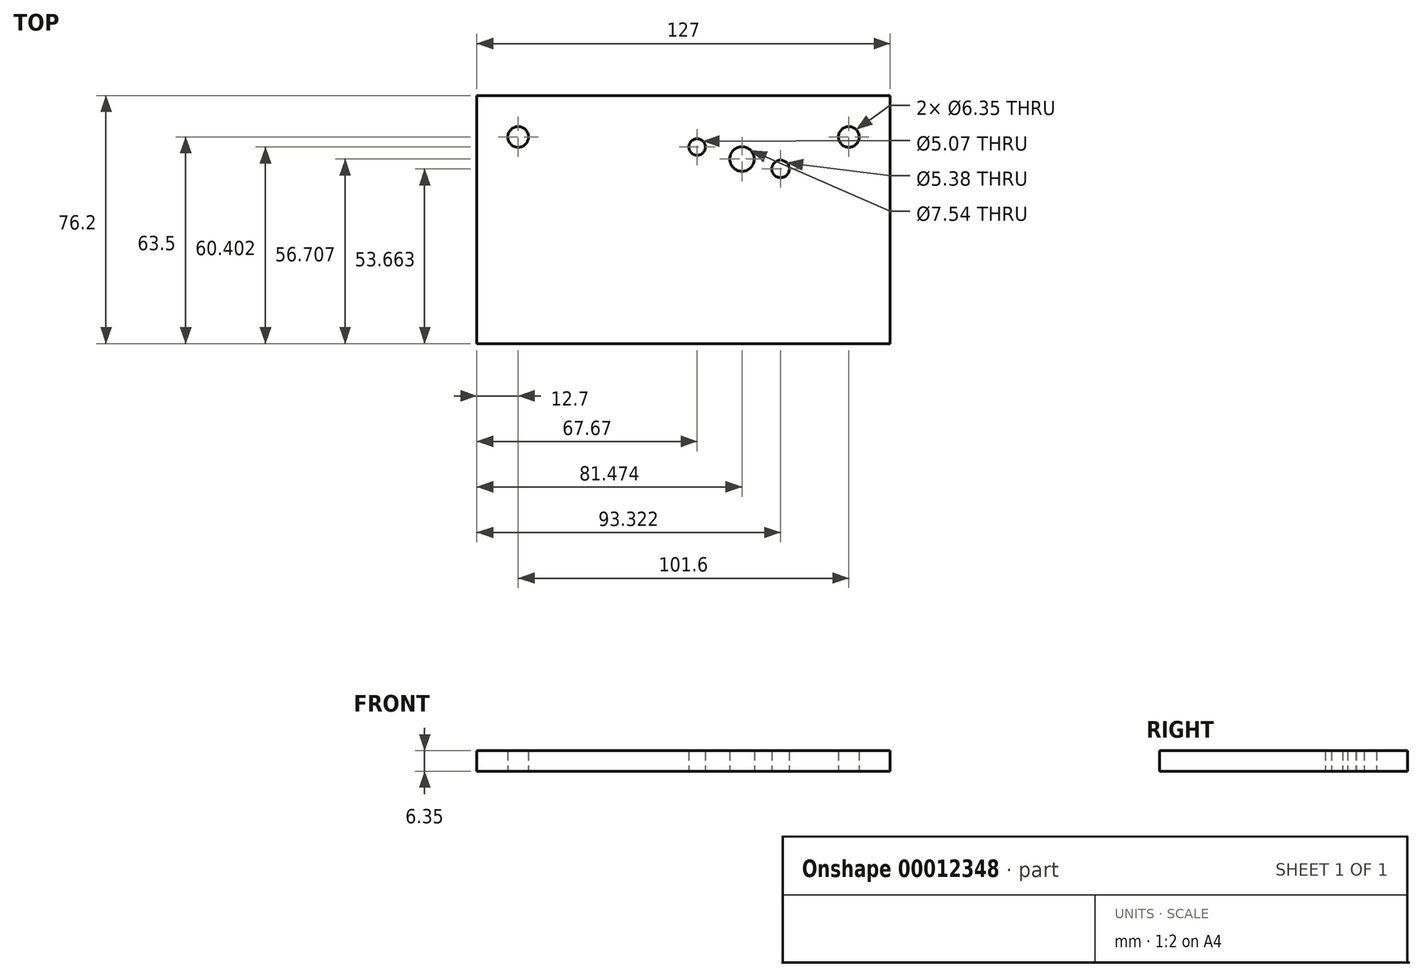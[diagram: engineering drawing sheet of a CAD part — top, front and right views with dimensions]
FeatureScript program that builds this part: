
annotation { "Feature Type Name" : "Feature", "Feature Type Description" : "" }
export const myFeature = defineFeature(function(context is Context, id is Id, definition is map)
    precondition{}
    {
        {
            var Q0;
            Q0=qCreatedBy(makeId("Top.planeOp"),FACE);
            var sketch = newSketch(context, id + "F0", { "sketchPlane" : qUnion([Q0])});
            skLineSegment(sketch, "E0.bottom", {"start": v(12.7, 12.7) * mm, "end": v(-114.3, 12.7) * mm});
            skLineSegment(sketch, "E0.top", {"start": v(12.7, -63.5) * mm, "end": v(-114.3, -63.5) * mm});
            skLineSegment(sketch, "E0.left", {"start": v(12.7, 12.7) * mm, "end": v(12.7, -63.5) * mm});
            skLineSegment(sketch, "E0.right", {"start": v(-114.3, 12.7) * mm, "end": v(-114.3, -63.5) * mm});
            skCircle(sketch, "E1", {"center": v(0, 0) * mm, "radius": 3.18 * mm});
            skCircle(sketch, "E2", {"center": v(-32.83, -6.8) * mm, "radius": 3.77 * mm});
            skCircle(sketch, "E3", {"center": v(-20.98, -9.84) * mm, "radius": 2.7 * mm});
            skCircle(sketch, "E4", {"center": v(-46.63, -3.1) * mm, "radius": 2.54 * mm});
            skCircle(sketch, "E5", {"center": v(-101.6, 0) * mm, "radius": 3.18 * mm});
            skSolve(sketch);
        }
        {
            var Q0;
            Q0 = qSketchRegion(id + "F0", true);
            extrude(context, id + "F1", {"entities" : qUnion([Q0]), "depth" : 6.35 * mm});
        }
    });
